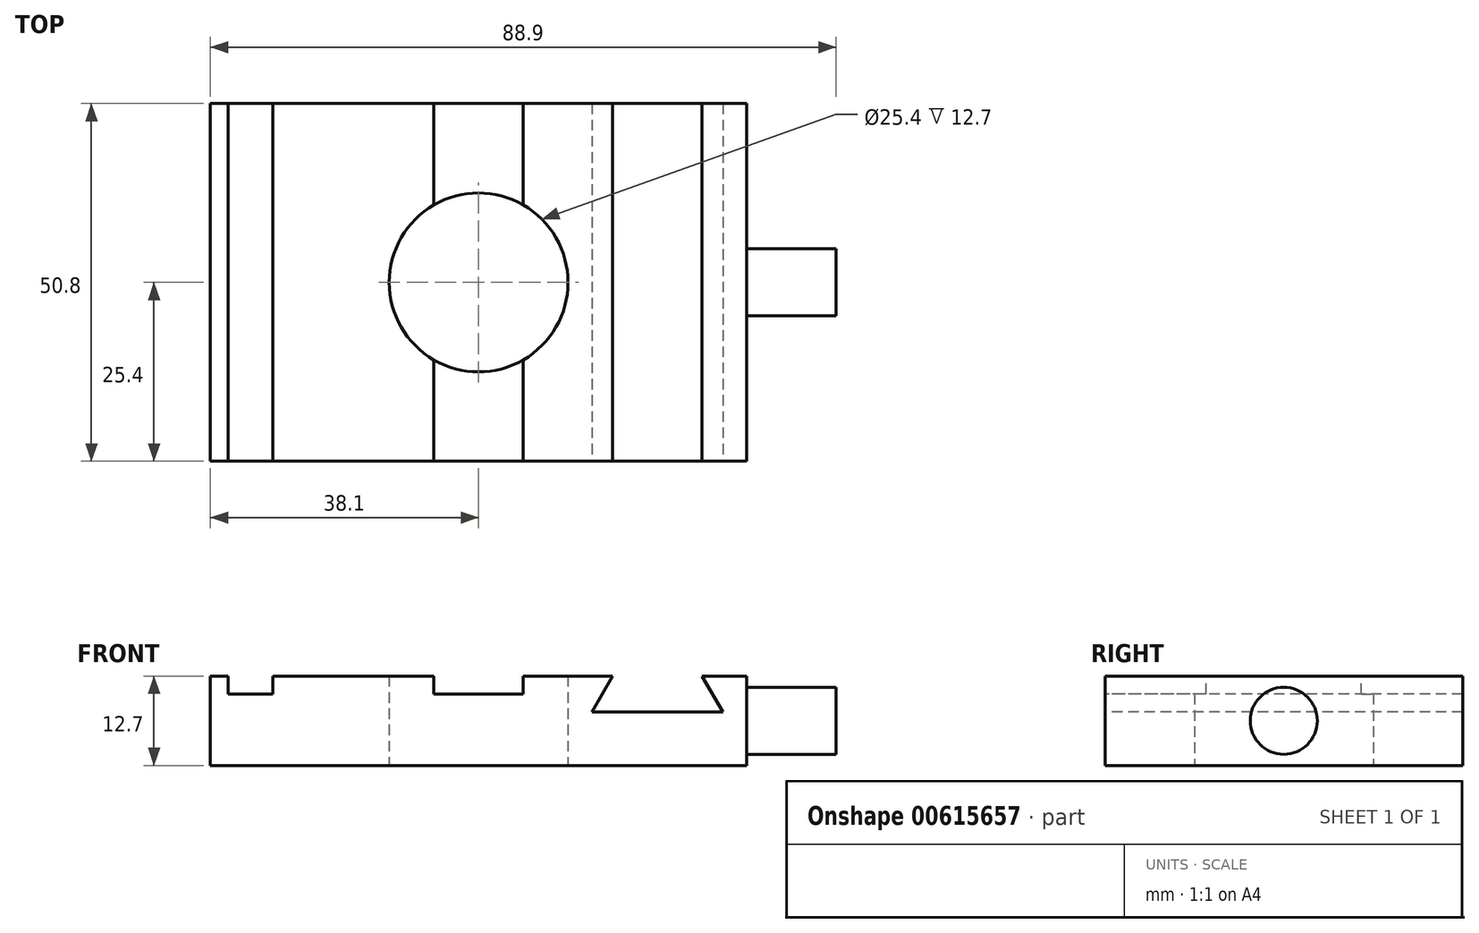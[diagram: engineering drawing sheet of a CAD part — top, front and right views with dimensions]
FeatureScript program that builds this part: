
annotation { "Feature Type Name" : "Feature", "Feature Type Description" : "" }
export const myFeature = defineFeature(function(context is Context, id is Id, definition is map)
    precondition{}
    {
        {
            var Q0;
            Q0=qCreatedBy(makeId("Top.planeOp"),FACE);
            var sketch = newSketch(context, id + "F0", { "sketchPlane" : qUnion([Q0])});
            skLineSegment(sketch, "E0.bottom", {"start": v(-38.1, 25.4) * mm, "end": v(38.1, 25.4) * mm});
            skLineSegment(sketch, "E0.top", {"start": v(-38.1, -25.4) * mm, "end": v(38.1, -25.4) * mm});
            skLineSegment(sketch, "E0.left", {"start": v(-38.1, 25.4) * mm, "end": v(-38.1, -25.4) * mm});
            skLineSegment(sketch, "E0.right", {"start": v(38.1, 25.4) * mm, "end": v(38.1, -25.4) * mm});
            skPoint(sketch, "E0.middle", {"position": v(0, 0) * mm});
            skCircle(sketch, "E1", {"center": v(0, 0) * mm, "radius": 12.7 * mm});
            skSolve(sketch);
        }
        {
            var Q0;
            Q0=makeQuery(id+"F0.imprint","IMPRINT",FACE,{"disambiguationData":[TD([[makeQuery(id+"F0.imprint","IMPRINT",EDGE,{"derivedFrom":sQuery(id+"F0.wireOp",EDGE,"E0.bottom")}),-1.0]])]});
            extrude(context, id + "F1", {"entities" : qUnion([Q0]), "depth" : 12.7 * mm, "offsetDistance" : 25.4 * mm});
        }
        {
            var Q0;
            Q0=makeQuery(id+"F1.opExtrude","CAP_FACE",FACE,{"disambiguationData":[OSD([sQuery(id+"F0.wireOp",EDGE,"E0.bottom"),sQuery(id+"F0.wireOp",EDGE,"E0.top"),sQuery(id+"F0.wireOp",EDGE,"E0.left"),sQuery(id+"F0.wireOp",EDGE,"E0.right"),sQuery(id+"F0.wireOp",EDGE,"E1")])],"isStart":false});
            var sketch = newSketch(context, id + "F2", { "sketchPlane" : qUnion([Q0])});
            skLineSegment(sketch, "E2.bottom", {"start": v(-35.56, 25.4) * mm, "end": v(-29.21, 25.4) * mm});
            skLineSegment(sketch, "E2.top", {"start": v(-35.56, -25.4) * mm, "end": v(-29.21, -25.4) * mm});
            skLineSegment(sketch, "E2.left", {"start": v(-35.56, 25.4) * mm, "end": v(-35.56, -25.4) * mm});
            skLineSegment(sketch, "E2.right", {"start": v(-29.21, 25.4) * mm, "end": v(-29.21, -25.4) * mm});
            skLineSegment(sketch, "E3", {"start": v(-6.35, 25.4) * mm, "end": v(-6.35, -25.4) * mm});
            skLineSegment(sketch, "E4", {"start": v(-6.35, -25.4) * mm, "end": v(6.35, -25.4) * mm});
            skLineSegment(sketch, "E5", {"start": v(6.35, -25.4) * mm, "end": v(6.35, 25.4) * mm});
            skLineSegment(sketch, "E6", {"start": v(6.35, 25.4) * mm, "end": v(-6.35, 25.4) * mm});
            skPoint(sketch, "E7", {"position": v(0, 0) * mm});
            skLineSegment(sketch, "E8", {"start": v(0, 25.4) * mm, "end": v(0, -25.4) * mm, "construction": true});
            skSolve(sketch);
        }
        {
            var Q0;
            Q0=makeQuery(id+"F2.imprint","IMPRINT",FACE,{"disambiguationData":[TD([[makeQuery(id+"F2.imprint","IMPRINT",EDGE,{"derivedFrom":sQuery(id+"F2.wireOp",EDGE,"E2.bottom")}),-1.0]])]});
            var Q1;
            {var subQ0=sQuery(id+"F2.wireOp",EDGE,"E4");Q1=makeQuery(id+"F2.imprint","IMPRINT",FACE,{"disambiguationData":[TD([[makeQuery(id+"F2.imprint","IMPRINT",EDGE,{"derivedFrom":subQ0}),1.0]])]});}
            var Q2;
            {var subQ0=sQuery(id+"F2.wireOp",EDGE,"E6");Q2=makeQuery(id+"F2.imprint","IMPRINT",FACE,{"disambiguationData":[TD([[makeQuery(id+"F2.imprint","IMPRINT",EDGE,{"derivedFrom":subQ0}),-1.0]])]});}
            extrude(context, id + "F3", {"entities" : qUnion([Q0, Q1, Q2]), "operationType" : NewBodyOperationType.REMOVE, "oppositeDirection" : true, "depth" : 2.54 * mm, "offsetDistance" : 25.4 * mm});
        }
        {
            var Q0;
            Q0=makeQuery(id+"F1.opExtrude","SWEPT_FACE",FACE,{"disambiguationData":[OSD([sQuery(id+"F0.wireOp",EDGE,"E0.top")])]});
            var sketch = newSketch(context, id + "F4", { "sketchPlane" : qUnion([Q0])});
            skLineSegment(sketch, "E9", {"start": v(19.05, 12.7) * mm, "end": v(16.12, 7.62) * mm});
            skLineSegment(sketch, "E10", {"start": v(16.12, 7.62) * mm, "end": v(34.68, 7.62) * mm});
            skLineSegment(sketch, "E11", {"start": v(34.68, 7.62) * mm, "end": v(31.75, 12.7) * mm});
            skLineSegment(sketch, "E12", {"start": v(31.75, 12.7) * mm, "end": v(19.05, 12.7) * mm});
            skLineSegment(sketch, "E13", {"start": v(25.4, 7.62) * mm, "end": v(25.4, 12.7) * mm, "construction": true});
            skSolve(sketch);
        }
        {
            var Q0;
            Q0=makeQuery(id+"F4.imprint","IMPRINT",FACE,{"disambiguationData":[TD([[makeQuery(id+"F4.imprint","IMPRINT",EDGE,{"derivedFrom":sQuery(id+"F4.wireOp",EDGE,"E9")}),1.0]])]});
            extrude(context, id + "F5", {"entities" : qUnion([Q0]), "operationType" : NewBodyOperationType.REMOVE, "endBound" : BoundingType.THROUGH_ALL, "oppositeDirection" : true, "depth" : 25.4 * mm, "offsetDistance" : 25.4 * mm});
        }
        {
            var Q0;
            Q0=makeQuery(id+"F1.opExtrude","SWEPT_FACE",FACE,{"disambiguationData":[OSD([sQuery(id+"F0.wireOp",EDGE,"E0.right")])]});
            var sketch = newSketch(context, id + "F6", { "sketchPlane" : qUnion([Q0])});
            skCircle(sketch, "E14", {"center": v(0, 6.35) * mm, "radius": 4.76 * mm});
            skPoint(sketch, "E14.centerSnap0", {"position": v(-25.4, 6.35) * mm});
            skPoint(sketch, "E14.centerSnap1", {"position": v(0, 12.7) * mm});
            skSolve(sketch);
        }
        {
            var Q0;
            Q0 = qSketchRegion(id + "F6", true);
            extrude(context, id + "F7", {"entities" : qUnion([Q0]), "operationType" : NewBodyOperationType.ADD, "depth" : 12.7 * mm, "offsetDistance" : 25.4 * mm});
        }
    });
